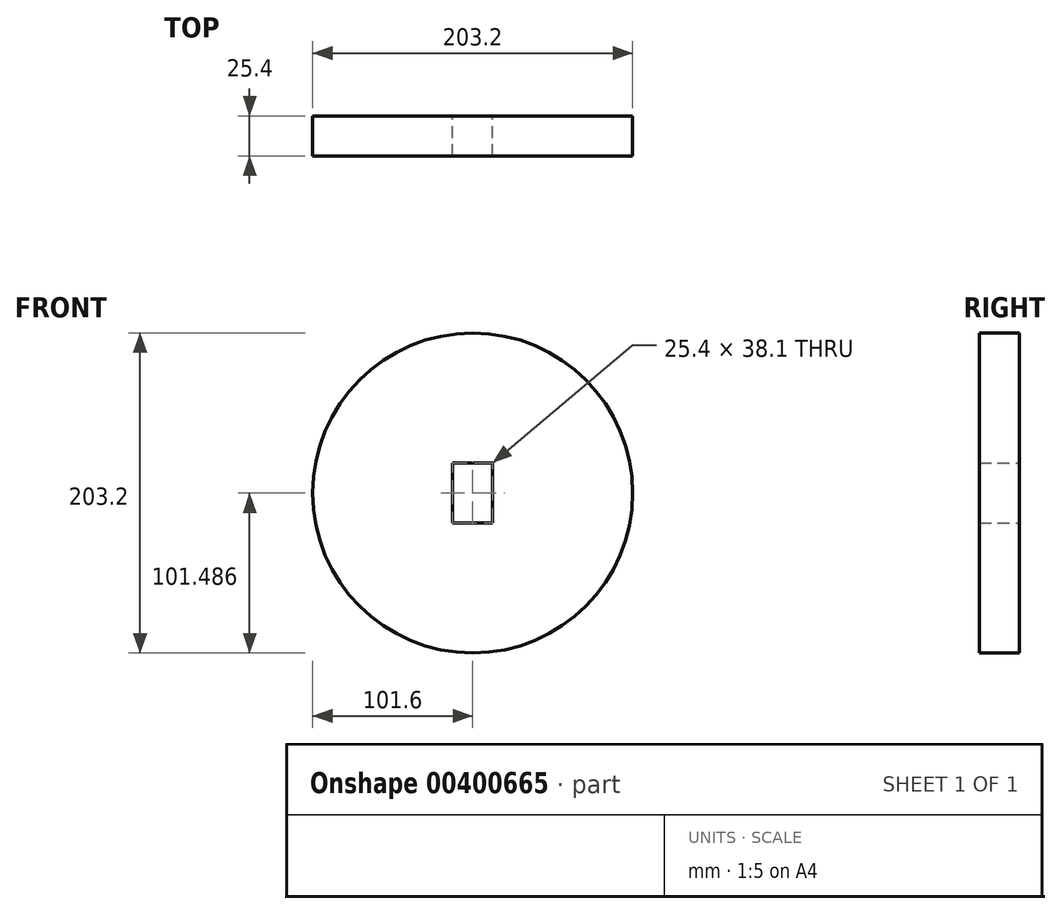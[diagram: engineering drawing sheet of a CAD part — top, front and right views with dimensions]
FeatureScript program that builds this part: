
annotation { "Feature Type Name" : "Feature", "Feature Type Description" : "" }
export const myFeature = defineFeature(function(context is Context, id is Id, definition is map)
    precondition{}
    {
        {
            var Q0;
            Q0=qCreatedBy(makeId("Front.planeOp"),FACE);
            var sketch = newSketch(context, id + "F0", { "sketchPlane" : qUnion([Q0])});
            skCircle(sketch, "E0", {"center": v(0, 0) * mm, "radius": 101.6 * mm});
            skLineSegment(sketch, "E1", {"start": v(-12.7, -0.11) * mm, "end": v(-12.7, -19.16) * mm});
            skLineSegment(sketch, "E2", {"start": v(-12.7, -0.11) * mm, "end": v(-12.7, 18.94) * mm});
            skLineSegment(sketch, "E3", {"start": v(-12.7, 18.94) * mm, "end": v(12.7, 18.94) * mm});
            skLineSegment(sketch, "E4", {"start": v(-12.7, -19.16) * mm, "end": v(12.7, -19.16) * mm});
            skLineSegment(sketch, "E5", {"start": v(-12.7, -0.11) * mm, "end": v(0, 0) * mm});
            skLineSegment(sketch, "E6", {"start": v(12.7, 0) * mm, "end": v(0, 0) * mm});
            skLineSegment(sketch, "E7", {"start": v(12.7, 18.94) * mm, "end": v(12.7, -19.16) * mm});
            skSolve(sketch);
        }
        {
            var Q0;
            Q0=makeQuery(id+"F0.imprint","IMPRINT",FACE,{"disambiguationData":[TD([[makeQuery(id+"F0.imprint","IMPRINT",EDGE,{"derivedFrom":sQuery(id+"F0.wireOp",EDGE,"E0")}),1.0]])]});
            extrude(context, id + "F1", {"entities" : qUnion([Q0]), "depth" : 25.4 * mm});
        }
    });
